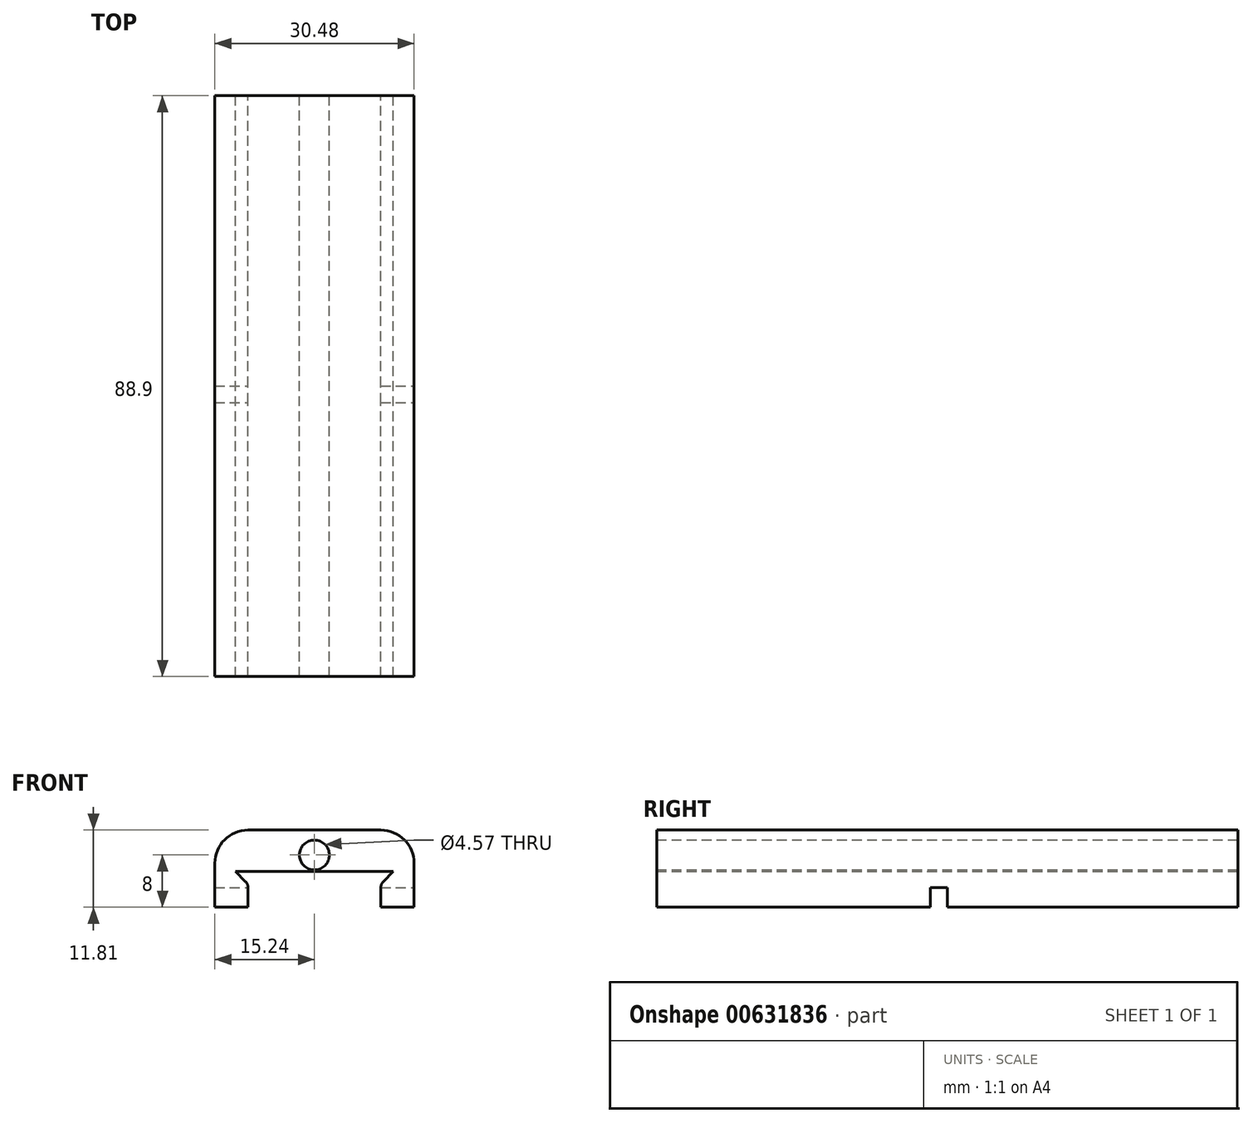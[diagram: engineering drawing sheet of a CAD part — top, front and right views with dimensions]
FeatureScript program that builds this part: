
annotation { "Feature Type Name" : "Feature", "Feature Type Description" : "" }
export const myFeature = defineFeature(function(context is Context, id is Id, definition is map)
    precondition{}
    {
        {
            var Q0;
            Q0=qCreatedBy(makeId("Front.planeOp"),FACE);
            var sketch = newSketch(context, id + "F0", { "sketchPlane" : qUnion([Q0])});
            skLineSegment(sketch, "E0", {"start": v(0, 0) * mm, "end": v(12.07, 0) * mm});
            skLineSegment(sketch, "E1", {"start": v(12.07, 0) * mm, "end": v(10.16, -1.9) * mm});
            skLineSegment(sketch, "E2", {"start": v(10.16, -1.9) * mm, "end": v(10.16, -5.46) * mm});
            skLineSegment(sketch, "E3", {"start": v(10.16, -5.46) * mm, "end": v(15.24, -5.46) * mm});
            skLineSegment(sketch, "E4", {"start": v(15.24, -5.46) * mm, "end": v(15.24, 6.35) * mm});
            skLineSegment(sketch, "E5", {"start": v(0, 6.35) * mm, "end": v(15.24, 6.35) * mm});
            skCircle(sketch, "E6", {"center": v(0, 2.54) * mm, "radius": 2.29 * mm});
            skPoint(sketch, "E7", {"position": v(0, 0) * mm});
            skPoint(sketch, "E8", {"position": v(0, 4.83) * mm});
            skLineSegment(sketch, "E9.MirrorCS", {"start": v(-12.07, 0) * mm, "end": v(-10.16, -1.9) * mm});
            skLineSegment(sketch, "E10.MirrorCS", {"start": v(-10.16, -1.9) * mm, "end": v(-10.16, -5.46) * mm});
            skLineSegment(sketch, "E11.MirrorCS", {"start": v(-10.16, -5.46) * mm, "end": v(-15.24, -5.46) * mm});
            skLineSegment(sketch, "E12.MirrorCS", {"start": v(-15.24, -5.46) * mm, "end": v(-15.24, 6.35) * mm});
            skLineSegment(sketch, "E13.MirrorCS", {"start": v(0, 6.35) * mm, "end": v(-15.24, 6.35) * mm});
            skLineSegment(sketch, "E14.MirrorCS", {"start": v(0, 0) * mm, "end": v(-12.07, 0) * mm});
            skPoint(sketch, "E15", {"position": v(0, 0.25) * mm});
            skSolve(sketch);
        }
        {
            var Q0;
            Q0 = qSketchRegion(id + "F0", true);
            extrude(context, id + "F1", {"entities" : qUnion([Q0]), "depth" : 88.9 * mm, "offsetDistance" : 25.4 * mm});
        }
        {
            var Q0;
            Q0=makeQuery(id+"F1.opExtrude","SWEPT_EDGE",EDGE,{"disambiguationData":[OSD([sQuery(id+"F0.wireOp",EDGE,"E9.MirrorCS"),sQuery(id+"F0.wireOp",EDGE,"E10.MirrorCS")])]});
            var Q1;
            Q1=makeQuery(id+"F1.opExtrude","SWEPT_EDGE",EDGE,{"disambiguationData":[OSD([sQuery(id+"F0.wireOp",EDGE,"E1"),sQuery(id+"F0.wireOp",EDGE,"E2")])]});
            fillet(context, id + "F2", {"entities" : qUnion([Q0, Q1]), "radius" : 1.27 * mm, "tangentPropagation" : true, "allowEdgeOverflow" : false});
        }
        {
            var Q0;
            Q0=makeQuery(id+"F1.opExtrude","SWEPT_EDGE",EDGE,{"disambiguationData":[OSD([sQuery(id+"F0.wireOp",EDGE,"E12.MirrorCS"),sQuery(id+"F0.wireOp",EDGE,"E13.MirrorCS")])]});
            var Q1;
            Q1=makeQuery(id+"F1.opExtrude","SWEPT_EDGE",EDGE,{"disambiguationData":[OSD([sQuery(id+"F0.wireOp",EDGE,"E4"),sQuery(id+"F0.wireOp",EDGE,"E5")])]});
            fillet(context, id + "F3", {"entities" : qUnion([Q0, Q1]), "radius" : 5.08 * mm, "tangentPropagation" : true, "allowEdgeOverflow" : false});
        }
        {
            var Q0;
            Q0=makeQuery(id+"F1.opExtrude","SWEPT_FACE",FACE,{"disambiguationData":[OSD([sQuery(id+"F0.wireOp",EDGE,"E10.MirrorCS")])]});
            var sketch = newSketch(context, id + "F4", { "sketchPlane" : qUnion([Q0])});
            skLineSegment(sketch, "E16.bottom", {"start": v(-47, -2.43) * mm, "end": v(-44.45, -2.43) * mm});
            skLineSegment(sketch, "E16.top", {"start": v(-47, -5.46) * mm, "end": v(-44.45, -5.46) * mm});
            skLineSegment(sketch, "E16.left", {"start": v(-47, -2.43) * mm, "end": v(-47, -5.46) * mm});
            skLineSegment(sketch, "E16.right", {"start": v(-44.45, -2.43) * mm, "end": v(-44.45, -5.46) * mm});
            skSolve(sketch);
        }
        {
            var Q0;
            Q0 = qSketchRegion(id + "F4", true);
            extrude(context, id + "F5", {"entities" : qUnion([Q0]), "operationType" : NewBodyOperationType.REMOVE, "endBound" : BoundingType.THROUGH_ALL, "oppositeDirection" : true, "depth" : 25.4 * mm, "offsetDistance" : 25.4 * mm, "hasSecondDirection" : true, "secondDirectionBound" : SecondDirectionBoundingType.THROUGH_ALL, "secondDirectionOppositeDirection" : false, "secondDirectionDepth" : 25.4 * mm});
        }
    });
